# Revit family: PFRID-ACPMK
name_source: partatom
category: Lighting Fixtures
units: mm (PartAtom-declared; Revit-internal decimal feet)

## family parameters
Cut with Voids When Loaded = Yes
Host = Face
Light Source = Yes
Maintain Annotation Orientation = No
Part Type = Normal
Room Calculation Point = No
Round Connector Dimension = Use Diameter
Shared = No

## types (1)
- PFRID35-120W-3000K-ACPMK
    A = 0' - 6 29/32"
    CRI = 90
    Color Filter = 16777215
    Default Elevation = 0' - 0"
    Dimming Lamp Color Temperature Shift = <None>
    Input Voltage = 120-277V
    Lamp = LED
    Lens = 1' - 5 7/16"
    Load Classification = Lighting
    Manufacturer = Above All Lighting
    Model = PFRID35-120-30901-ACPMK-WH
    Note = Max. Aircraft Cable and Wire Cord Length: 59" (1500mm).
    Photometric Web File = PFRID35-120W-3000K-Down.IES
    Power Factor = 0.9
    R = 1' - 5 11/16"
    Suspended = 3' - 0"
    Tilt Angle = 90.00°
    URL = https://www.abovealllighting.com
    Uplight R = 0' - 8 27/32"
    Wattage Comments = 120W
    r = 0' - 5 29/32"

## geometry (parser evidence)
native form markers: Sweep x9
no freeform markers — native parametric forms only
